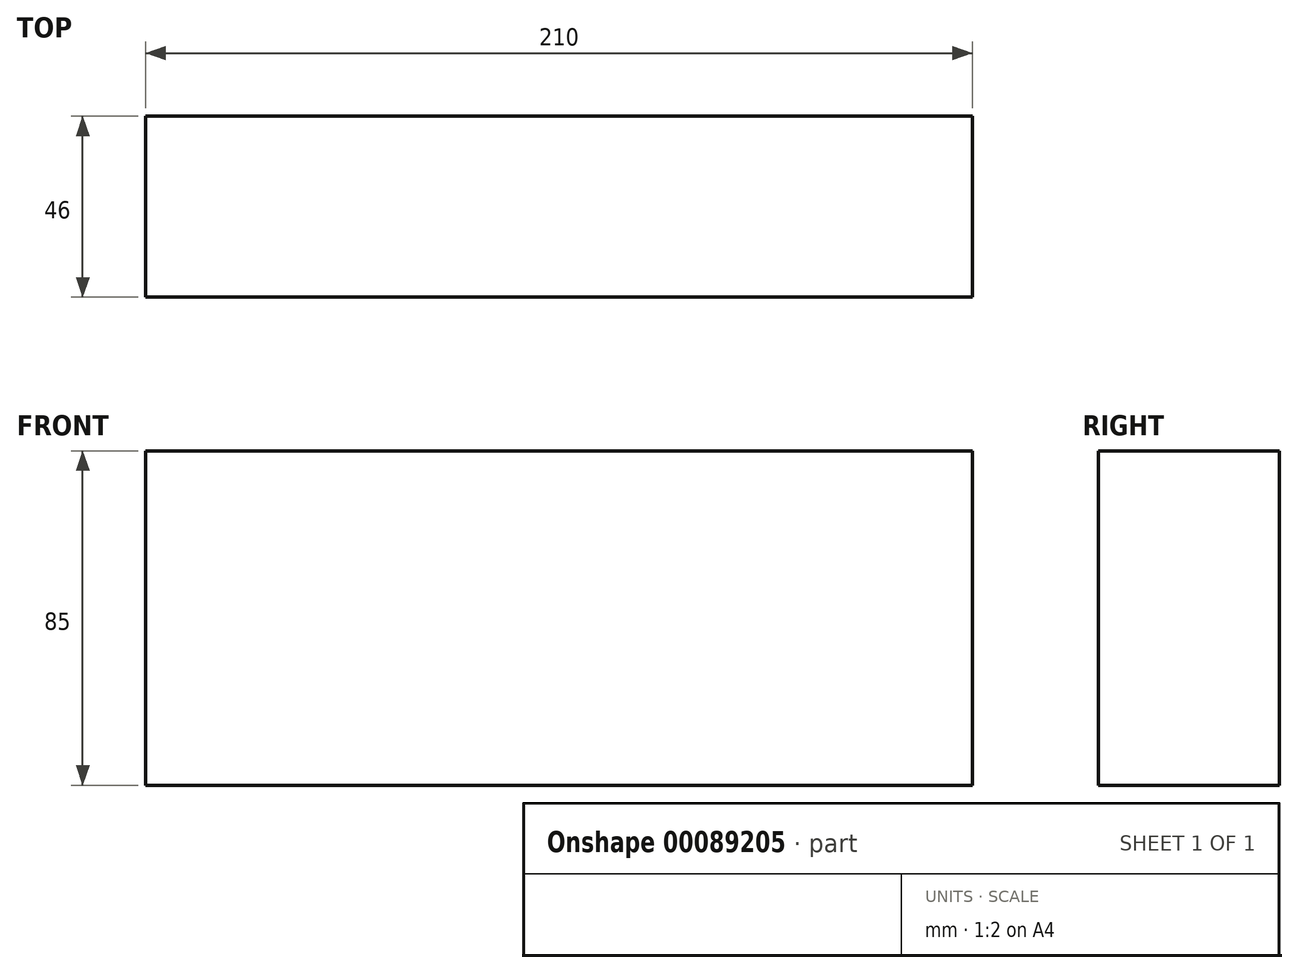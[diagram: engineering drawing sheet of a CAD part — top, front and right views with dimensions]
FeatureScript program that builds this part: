
annotation { "Feature Type Name" : "Feature", "Feature Type Description" : "" }
export const myFeature = defineFeature(function(context is Context, id is Id, definition is map)
    precondition{}
    {
        {
            var Q0;
            Q0=qCreatedBy(makeId("Front.planeOp"),FACE);
            var sketch = newSketch(context, id + "F0", { "sketchPlane" : qUnion([Q0])});
            skLineSegment(sketch, "E0.bottom", {"start": v(0, 0) * mm, "end": v(210, 0) * mm});
            skLineSegment(sketch, "E0.top", {"start": v(0, 85) * mm, "end": v(210, 85) * mm});
            skLineSegment(sketch, "E0.left", {"start": v(0, 0) * mm, "end": v(0, 85) * mm});
            skLineSegment(sketch, "E0.right", {"start": v(210, 0) * mm, "end": v(210, 85) * mm});
            skSolve(sketch);
        }
        {
            var Q0;
            Q0=makeQuery(id+"F0.imprint","IMPRINT",FACE,{"disambiguationData":[TD([[makeQuery(id+"F0.imprint","IMPRINT",EDGE,{"derivedFrom":sQuery(id+"F0.wireOp",EDGE,"E0.bottom")}),1.0]])]});
            extrude(context, id + "F1", {"entities" : qUnion([Q0]), "depth" : 46 * mm});
        }
    });
